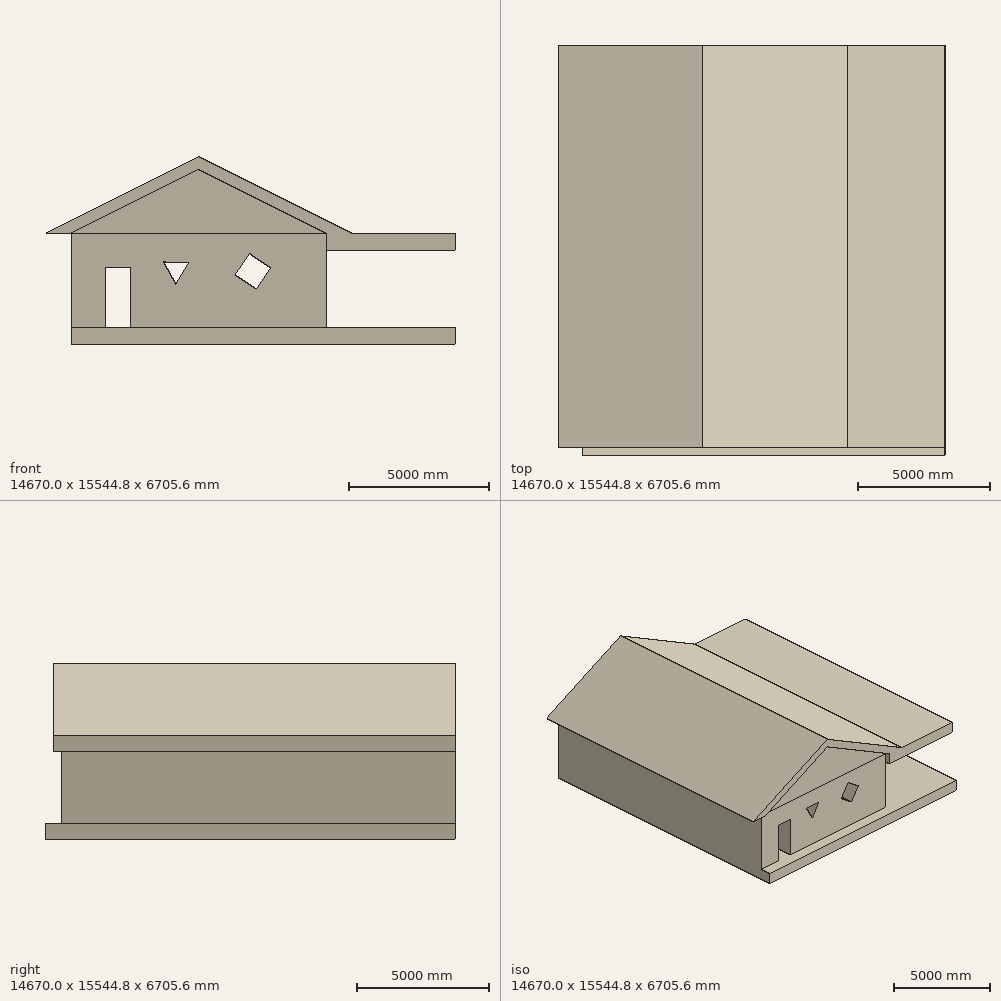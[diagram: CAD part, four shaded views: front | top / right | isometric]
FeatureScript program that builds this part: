
annotation { "Feature Type Name" : "Feature", "Feature Type Description" : "" }
export const myFeature = defineFeature(function(context is Context, id is Id, definition is map)
    precondition{}
    {
        {
            var Q0;
            Q0=qCreatedBy(makeId("Front.planeOp"),FACE);
            var sketch = newSketch(context, id + "F0", { "sketchPlane" : qUnion([Q0])});
            skLineSegment(sketch, "E0", {"start": v(0, 0) * mm, "end": v(4572, 0) * mm});
            skLineSegment(sketch, "E1", {"start": v(0, 0) * mm, "end": v(-4572, 0) * mm});
            skLineSegment(sketch, "E2", {"start": v(0, 0) * mm, "end": v(0, 2286) * mm});
            skLineSegment(sketch, "E3", {"start": v(0, 2286) * mm, "end": v(4572, 0) * mm});
            skLineSegment(sketch, "E4", {"start": v(0, 2286) * mm, "end": v(-4572, 0) * mm});
            skLineSegment(sketch, "E5", {"start": v(-4572, 0) * mm, "end": v(-5486.4, 0) * mm});
            skLineSegment(sketch, "E6", {"start": v(0, 2286) * mm, "end": v(0, 2743.2) * mm});
            skLineSegment(sketch, "E7", {"start": v(-5486.4, 0) * mm, "end": v(0, 2743.2) * mm});
            skLineSegment(sketch, "E8", {"start": v(4572, 0) * mm, "end": v(5486.4, 0) * mm});
            skLineSegment(sketch, "E9", {"start": v(5486.4, 0) * mm, "end": v(0, 2743.2) * mm});
            skLineSegment(sketch, "E10", {"start": v(-4572, 0) * mm, "end": v(-4572, -3352.8) * mm});
            skLineSegment(sketch, "E11", {"start": v(-4572, -3352.8) * mm, "end": v(4572, -3352.8) * mm});
            skLineSegment(sketch, "E12", {"start": v(4572, -3352.8) * mm, "end": v(4572, 0) * mm});
            skLineSegment(sketch, "E13", {"start": v(-4572, -3352.8) * mm, "end": v(-4572, -3962.4) * mm});
            skLineSegment(sketch, "E14", {"start": v(-4572, -3962.4) * mm, "end": v(4572, -3962.4) * mm});
            skLineSegment(sketch, "E15", {"start": v(4572, -3962.4) * mm, "end": v(4572, -3352.8) * mm});
            skPoint(sketch, "E16", {"position": v(4572, -1676.4) * mm});
            skLineSegment(sketch, "E17", {"start": v(4572, 0) * mm, "end": v(9183.62, 0) * mm});
            skLineSegment(sketch, "E18", {"start": v(9183.62, 0) * mm, "end": v(9183.62, -609.6) * mm});
            skLineSegment(sketch, "E19", {"start": v(9183.62, -609.6) * mm, "end": v(4572, -609.6) * mm});
            skLineSegment(sketch, "E20", {"start": v(4572, -609.6) * mm, "end": v(4572, 0) * mm});
            skLineSegment(sketch, "E21", {"start": v(4572, -3352.8) * mm, "end": v(9183.62, -3352.8) * mm});
            skLineSegment(sketch, "E22", {"start": v(9183.62, -3352.8) * mm, "end": v(9183.62, -3962.4) * mm});
            skLineSegment(sketch, "E23", {"start": v(9183.62, -3962.4) * mm, "end": v(4572, -3962.4) * mm});
            skLineSegment(sketch, "E24", {"start": v(9183.62, -3352.8) * mm, "end": v(9183.62, -609.6) * mm});
            skLineSegment(sketch, "E25", {"start": v(-3352.8, -3352.8) * mm, "end": v(-3352.8, -1219.2) * mm});
            skLineSegment(sketch, "E26", {"start": v(-3352.8, -1219.2) * mm, "end": v(-2438.4, -1219.2) * mm});
            skLineSegment(sketch, "E27", {"start": v(-2438.4, -1219.2) * mm, "end": v(-2438.4, -3352.8) * mm});
            skLineSegment(sketch, "E28", {"start": v(1819.42, -726.45) * mm, "end": v(1305.99, -1483.1) * mm});
            skLineSegment(sketch, "E29", {"start": v(1305.99, -1483.1) * mm, "end": v(2062.63, -1996.53) * mm});
            skLineSegment(sketch, "E30", {"start": v(2062.63, -1996.53) * mm, "end": v(2576.07, -1239.89) * mm});
            skLineSegment(sketch, "E31", {"start": v(2576.07, -1239.89) * mm, "end": v(1819.42, -726.45) * mm});
            skLineSegment(sketch, "E32", {"start": v(-1261.55, -1019.88) * mm, "end": v(-815.18, -1817.93) * mm});
            skLineSegment(sketch, "E33", {"start": v(-815.18, -1817.93) * mm, "end": v(-347.24, -1032.34) * mm});
            skLineSegment(sketch, "E34", {"start": v(-347.24, -1032.34) * mm, "end": v(-1261.55, -1019.88) * mm});
            skLineSegment(sketch, "E35", {"start": v(7355.31, -1075.44) * mm, "end": v(6440.91, -1075.44) * mm});
            skLineSegment(sketch, "E36", {"start": v(6440.91, -1075.44) * mm, "end": v(6003.52, -1878.45) * mm});
            skLineSegment(sketch, "E37", {"start": v(6003.52, -1878.45) * mm, "end": v(6440.91, -2681.45) * mm});
            skLineSegment(sketch, "E38", {"start": v(6440.91, -2681.45) * mm, "end": v(7355.31, -2681.45) * mm});
            skLineSegment(sketch, "E39", {"start": v(7355.31, -2681.45) * mm, "end": v(7792.7, -1878.45) * mm});
            skLineSegment(sketch, "E40", {"start": v(7792.7, -1878.45) * mm, "end": v(7355.31, -1075.44) * mm});
            skSolve(sketch);
        }
        {
            var Q0;
            Q0=makeQuery(id+"F0.imprint","IMPRINT",FACE,{"disambiguationData":[TD([[makeQuery(id+"F0.imprint","IMPRINT",EDGE,{"derivedFrom":sQuery(id+"F0.wireOp",EDGE,"E4")}),-1.0]])]});
            var Q1;
            {var subQ0=sQuery(id+"F0.wireOp",EDGE,"E3");Q1=makeQuery(id+"F0.imprint","IMPRINT",FACE,{"disambiguationData":[TD([[makeQuery(id+"F0.imprint","IMPRINT",EDGE,{"derivedFrom":subQ0}),1.0]])]});}
            var Q2;
            {var subQ0=sQuery(id+"F0.wireOp",EDGE,"E18");Q2=makeQuery(id+"F0.imprint","IMPRINT",FACE,{"disambiguationData":[TD([[makeQuery(id+"F0.imprint","IMPRINT",EDGE,{"derivedFrom":subQ0}),-1.0]])]});}
            extrude(context, id + "F1", {"entities" : qUnion([Q0, Q1, Q2]), "depth" : 15240 * mm, "offsetDistance" : 30.48 * mm});
        }
        {
            var Q0;
            Q0=makeQuery(id+"F0.imprint","IMPRINT",FACE,{"disambiguationData":[TD([[makeQuery(id+"F0.imprint","IMPRINT",EDGE,{"derivedFrom":sQuery(id+"F0.wireOp",EDGE,"E1")}),-1.0]])]});
            var Q1;
            Q1=makeQuery(id+"F0.imprint","IMPRINT",FACE,{"disambiguationData":[TD([[makeQuery(id+"F0.imprint","IMPRINT",EDGE,{"derivedFrom":sQuery(id+"F0.wireOp",EDGE,"E0")}),1.0]])]});
            extrude(context, id + "F2", {"entities" : qUnion([Q0, Q1]), "operationType" : NewBodyOperationType.ADD, "depth" : 15087.6 * mm, "offsetDistance" : 30.48 * mm});
        }
        {
            var Q0;
            Q0=makeQuery(id+"F0.imprint","IMPRINT",FACE,{"disambiguationData":[TD([[makeQuery(id+"F0.imprint","IMPRINT",EDGE,{"derivedFrom":sQuery(id+"F0.wireOp",EDGE,"E0")}),-1.0]])]});
            var Q1;
            Q1=makeQuery(id+"F0.imprint","IMPRINT",FACE,{"disambiguationData":[TD([[makeQuery(id+"F0.imprint","IMPRINT",EDGE,{"derivedFrom":sQuery(id+"F0.wireOp",EDGE,"E12")}),-1.0]])]});
            extrude(context, id + "F3", {"entities" : qUnion([Q0, Q1]), "operationType" : NewBodyOperationType.ADD, "depth" : 14935.2 * mm, "offsetDistance" : 30.48 * mm});
        }
        {
            var Q0;
            {var subQ0=sQuery(id+"F0.wireOp",EDGE,"E13");Q0=makeQuery(id+"F0.imprint","IMPRINT",FACE,{"disambiguationData":[TD([[makeQuery(id+"F0.imprint","IMPRINT",EDGE,{"derivedFrom":subQ0}),1.0]])]});}
            var Q1;
            Q1=makeQuery(id+"F0.imprint","IMPRINT",FACE,{"disambiguationData":[TD([[makeQuery(id+"F0.imprint","IMPRINT",EDGE,{"derivedFrom":sQuery(id+"F0.wireOp",EDGE,"E15")}),-1.0]])]});
            extrude(context, id + "F4", {"entities" : qUnion([Q0, Q1]), "operationType" : NewBodyOperationType.ADD, "depth" : 15544.8 * mm, "offsetDistance" : 30.48 * mm});
        }
    });
